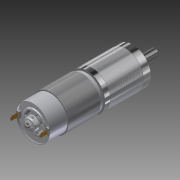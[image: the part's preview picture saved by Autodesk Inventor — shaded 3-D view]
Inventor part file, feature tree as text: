
AUTODESK INVENTOR PART (.ipt)
format: ipt  version: 2014 (Build 180170000, 170)  size: 340,992 bytes
history: native  units: in
note: dims shown in document units (in); Inventor stores cm internally (conversion verified against a paired STEP export)
features: mirror x1, other x1, imported_body x1
ambient origin geometry x8: Origin, YZ Plane, XZ Plane, XY Plane, X Axis, Y Axis, Z Axis, Center Point
bodies: Body1 (feature_tree)
feature tree (3):
  mirror  "Mirror2"
  other  "PG-711"
  imported_body  "Base1"
